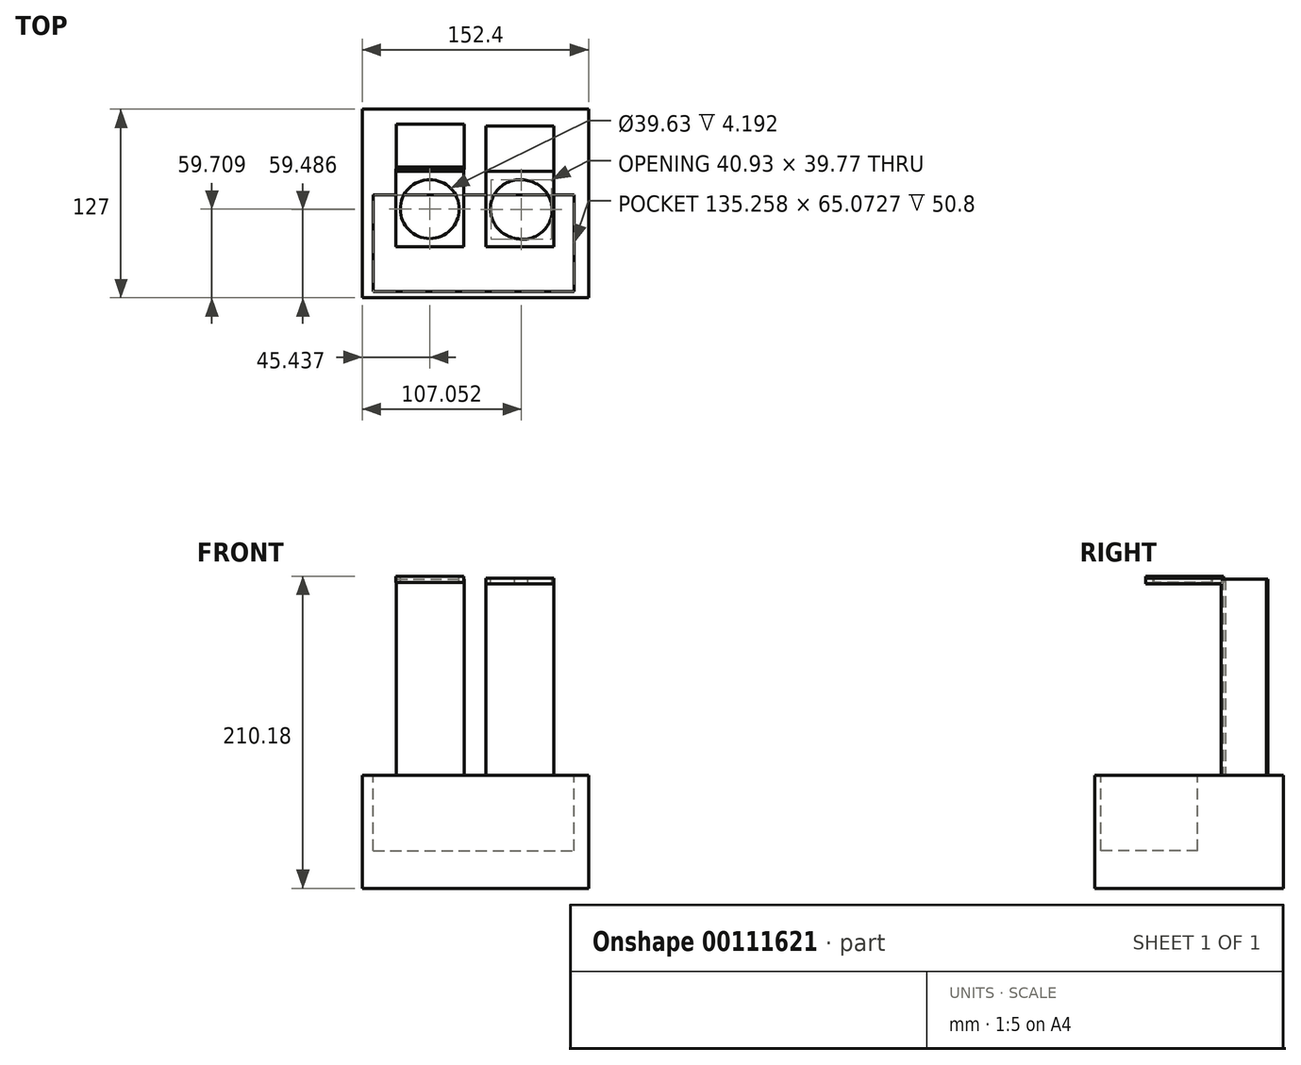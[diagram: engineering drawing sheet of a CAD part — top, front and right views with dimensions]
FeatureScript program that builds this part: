
annotation { "Feature Type Name" : "Feature", "Feature Type Description" : "" }
export const myFeature = defineFeature(function(context is Context, id is Id, definition is map)
    precondition{}
    {
        {
            var Q0;
            Q0=qCreatedBy(makeId("Top.planeOp"),FACE);
            var sketch = newSketch(context, id + "F0", { "sketchPlane" : qUnion([Q0])});
            skLineSegment(sketch, "E0.bottom", {"start": v(-56.17, 48.99) * mm, "end": v(96.23, 48.99) * mm});
            skLineSegment(sketch, "E0.top", {"start": v(-56.17, -78.01) * mm, "end": v(96.23, -78.01) * mm});
            skLineSegment(sketch, "E0.left", {"start": v(-56.17, 48.99) * mm, "end": v(-56.17, -78.01) * mm});
            skLineSegment(sketch, "E0.right", {"start": v(96.23, 48.99) * mm, "end": v(96.23, -78.01) * mm});
            skSolve(sketch);
        }
        {
            var Q0;
            Q0=makeQuery(id+"F0.imprint","IMPRINT",FACE,{"disambiguationData":[TD([[makeQuery(id+"F0.imprint","IMPRINT",EDGE,{"derivedFrom":sQuery(id+"F0.wireOp",EDGE,"E0.bottom")}),-1.0]])]});
            extrude(context, id + "F1", {"entities" : qUnion([Q0]), "depth" : 76.2 * mm});
        }
        {
            var Q0;
            Q0=makeQuery(id+"F1.opExtrude","CAP_FACE",FACE,{"disambiguationData":[OSD([sQuery(id+"F0.wireOp",EDGE,"E0.bottom"),sQuery(id+"F0.wireOp",EDGE,"E0.top"),sQuery(id+"F0.wireOp",EDGE,"E0.left"),sQuery(id+"F0.wireOp",EDGE,"E0.right")])],"isStart":false});
            var sketch = newSketch(context, id + "F2", { "sketchPlane" : qUnion([Q0])});
            skLineSegment(sketch, "E1.bottom", {"start": v(-48.79, -8.6) * mm, "end": v(86.47, -8.6) * mm});
            skLineSegment(sketch, "E1.top", {"start": v(-48.79, -73.67) * mm, "end": v(86.47, -73.67) * mm});
            skLineSegment(sketch, "E1.left", {"start": v(-48.79, -8.6) * mm, "end": v(-48.79, -73.67) * mm});
            skLineSegment(sketch, "E1.right", {"start": v(86.47, -8.6) * mm, "end": v(86.47, -73.67) * mm});
            skSolve(sketch);
        }
        {
            var Q0;
            Q0=makeQuery(id+"F2.imprint","IMPRINT",FACE,{"disambiguationData":[TD([[makeQuery(id+"F2.imprint","IMPRINT",EDGE,{"derivedFrom":sQuery(id+"F2.wireOp",EDGE,"E1.bottom")}),-1.0]])]});
            extrude(context, id + "F3", {"entities" : qUnion([Q0]), "operationType" : NewBodyOperationType.REMOVE, "oppositeDirection" : true, "depth" : 50.8 * mm});
        }
        {
            var Q0;
            Q0=makeQuery(id+"F1.opExtrude","CAP_FACE",FACE,{"disambiguationData":[OSD([sQuery(id+"F0.wireOp",EDGE,"E0.bottom"),sQuery(id+"F0.wireOp",EDGE,"E0.top"),sQuery(id+"F0.wireOp",EDGE,"E0.left"),sQuery(id+"F0.wireOp",EDGE,"E0.right")])],"isStart":false});
            var sketch = newSketch(context, id + "F4", { "sketchPlane" : qUnion([Q0])});
            skLineSegment(sketch, "E2.bottom", {"start": v(-33.21, 38.8) * mm, "end": v(12.5, 38.8) * mm});
            skLineSegment(sketch, "E2.top", {"start": v(-33.21, 8.32) * mm, "end": v(12.5, 8.32) * mm});
            skLineSegment(sketch, "E2.left", {"start": v(-33.21, 38.8) * mm, "end": v(-33.21, 8.32) * mm});
            skLineSegment(sketch, "E2.right", {"start": v(12.5, 38.8) * mm, "end": v(12.5, 8.32) * mm});
            skLineSegment(sketch, "E3.bottom", {"start": v(72.8, 37.58) * mm, "end": v(27.08, 37.58) * mm});
            skLineSegment(sketch, "E3.top", {"start": v(72.8, 7.1) * mm, "end": v(27.08, 7.1) * mm});
            skLineSegment(sketch, "E3.left", {"start": v(72.8, 37.58) * mm, "end": v(72.8, 7.1) * mm});
            skLineSegment(sketch, "E3.right", {"start": v(27.08, 37.58) * mm, "end": v(27.08, 7.1) * mm});
            skSolve(sketch);
        }
        {
            var Q0;
            Q0=makeQuery(id+"F4.imprint","IMPRINT",FACE,{"disambiguationData":[TD([[makeQuery(id+"F4.imprint","IMPRINT",EDGE,{"derivedFrom":sQuery(id+"F4.wireOp",EDGE,"E3.bottom")}),1.0]])]});
            var Q1;
            Q1=makeQuery(id+"F4.imprint","IMPRINT",FACE,{"disambiguationData":[TD([[makeQuery(id+"F4.imprint","IMPRINT",EDGE,{"derivedFrom":sQuery(id+"F4.wireOp",EDGE,"E2.bottom")}),-1.0]])]});
            extrude(context, id + "F5", {"entities" : qUnion([Q0, Q1]), "operationType" : NewBodyOperationType.ADD, "depth" : 132.08 * mm});
        }
        {
            var Q0;
            Q0=makeQuery(id+"F5.opExtrude","SWEPT_FACE",FACE,{"disambiguationData":[OSD([sQuery(id+"F4.wireOp",EDGE,"E3.top")])]});
            var sketch = newSketch(context, id + "F6", { "sketchPlane" : qUnion([Q0])});
            skLineSegment(sketch, "E4.bottom", {"start": v(-33.6, 210.18) * mm, "end": v(12.13, 210.18) * mm});
            skLineSegment(sketch, "E4.top", {"start": v(-33.6, 205.99) * mm, "end": v(12.13, 205.99) * mm});
            skLineSegment(sketch, "E4.left", {"start": v(-33.6, 210.18) * mm, "end": v(-33.6, 205.99) * mm});
            skLineSegment(sketch, "E4.right", {"start": v(12.13, 210.18) * mm, "end": v(12.13, 205.99) * mm});
            skLineSegment(sketch, "E5.bottom", {"start": v(27.08, 209) * mm, "end": v(72.8, 209) * mm});
            skLineSegment(sketch, "E5.top", {"start": v(27.08, 205.2) * mm, "end": v(72.8, 205.2) * mm});
            skLineSegment(sketch, "E5.left", {"start": v(27.08, 209) * mm, "end": v(27.08, 205.2) * mm});
            skLineSegment(sketch, "E5.right", {"start": v(72.8, 209) * mm, "end": v(72.8, 205.2) * mm});
            skSolve(sketch);
        }
        {
            var Q0;
            Q0 = qSketchRegion(id + "F6", true);
            extrude(context, id + "F7", {"entities" : qUnion([Q0]), "operationType" : NewBodyOperationType.ADD, "depth" : 50.8 * mm});
        }
        {
            var Q0;
            Q0=makeQuery(id+"F7.opExtrude","SWEPT_FACE",FACE,{"disambiguationData":[OSD([sQuery(id+"F6.wireOp",EDGE,"E4.bottom")])]});
            var sketch = newSketch(context, id + "F8", { "sketchPlane" : qUnion([Q0])});
            skCircle(sketch, "E6", {"center": v(-10.73, -18.3) * mm, "radius": 19.81 * mm});
            skCircle(sketch, "E7", {"center": v(51.83, -18.75) * mm, "radius": 19.81 * mm});
            skSolve(sketch);
        }
        {
            var Q0;
            Q0=makeQuery(id+"F8.imprint","IMPRINT",FACE,{"disambiguationData":[TD([[makeQuery(id+"F8.imprint","IMPRINT",EDGE,{"derivedFrom":sQuery(id+"F8.wireOp",EDGE,"E6")}),1.0]])]});
            var Q1;
            Q1=makeQuery(id+"F8.imprint","IMPRINT",FACE,{"disambiguationData":[TD([[makeQuery(id+"F8.imprint","IMPRINT",EDGE,{"derivedFrom":sQuery(id+"F8.wireOp",EDGE,"E7")}),1.0]])]});
            var Q2;
            Q2=sQuery(id+"F8.wireOp",EDGE,"E7");
            var Q3;
            Q3=sQuery(id+"F8.wireOp",EDGE,"E6");
            extrude(context, id + "F9", {"entities" : qUnion([Q0, Q1]), "operationType" : NewBodyOperationType.REMOVE, "surfaceEntities" : qUnion([Q2, Q3]), "oppositeDirection" : true, "depth" : 25.4 * mm});
        }
        {
            var Q0;
            Q0=makeQuery(id+"F7.opExtrude","SWEPT_FACE",FACE,{"disambiguationData":[OSD([sQuery(id+"F6.wireOp",EDGE,"E5.bottom")])]});
            var sketch = newSketch(context, id + "F10", { "sketchPlane" : qUnion([Q0])});
            skCircle(sketch, "E8", {"center": v(49.94, -18.3) * mm, "radius": 19.81 * mm});
            skSolve(sketch);
        }
        {
            var Q0;
            Q0=makeQuery(id+"F10.imprint","IMPRINT",FACE,{"disambiguationData":[TD([[makeQuery(id+"F10.imprint","IMPRINT",EDGE,{"derivedFrom":sQuery(id+"F10.wireOp",EDGE,"E8")}),1.0]])]});
            extrude(context, id + "F11", {"entities" : qUnion([Q0]), "operationType" : NewBodyOperationType.REMOVE, "oppositeDirection" : true, "depth" : 25.4 * mm});
        }
        {
            var Q0;
            Q0=makeQuery(id+"F7.opExtrude","CAP_FACE",FACE,{"disambiguationData":[OSD([sQuery(id+"F6.wireOp",EDGE,"E4.bottom"),sQuery(id+"F6.wireOp",EDGE,"E4.top"),sQuery(id+"F6.wireOp",EDGE,"E4.left"),sQuery(id+"F6.wireOp",EDGE,"E4.right")])],"isStart":true});
            var Q1;
            Q1=makeQuery(id+"F5.opExtrude","SWEPT_FACE",FACE,{"disambiguationData":[OSD([sQuery(id+"F4.wireOp",EDGE,"E2.top")])]});
            extrude(context, id + "F12", {"entities" : qUnion([Q0, Q1]), "depth" : 1.78 * mm});
        }
    });
